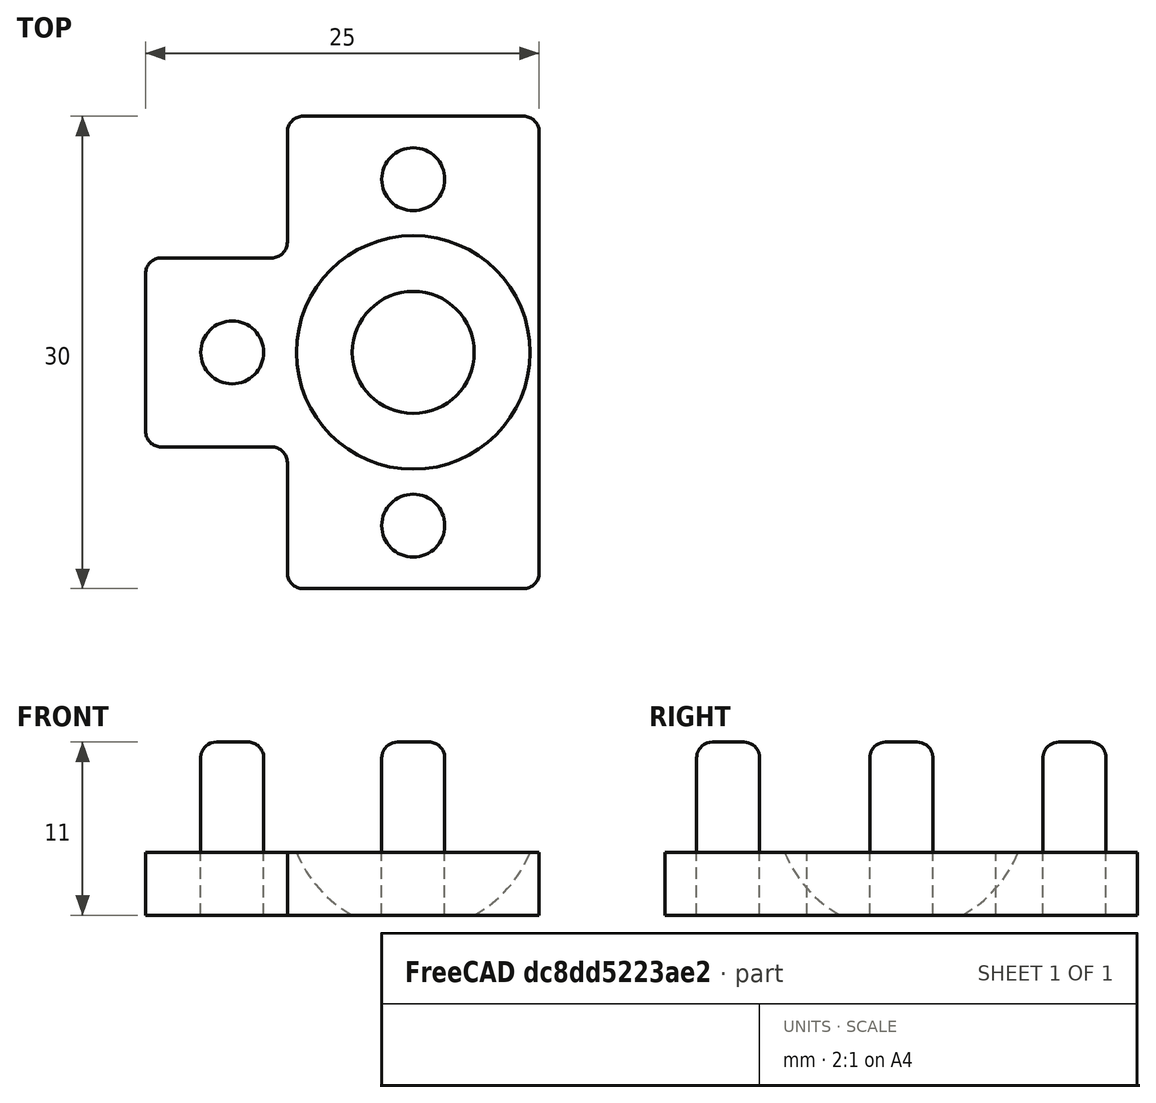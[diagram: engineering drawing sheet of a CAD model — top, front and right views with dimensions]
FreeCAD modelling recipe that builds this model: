
FCSTD DOCUMENT  (FreeCAD 0.20R29603 (Git))
Label: thing for marball
License: All rights reserved
LicenseURL: http://en.wikipedia.org/wiki/All_rights_reserved
objects: Part::Fillet×4, Part::Box×3, Part::Cylinder×3, Part::Cut×3, Part::Sphere×1
note: 14 computed .brp shape members not serialized (recipe doc carries the construction recipe); baked Part::Feature solids carry a one-line shape summary decoded from their .brp

FEATURE [Part::Box] Box  label="Cube"
  AttacherType = Attacher::AttachEngine3D
  Height = 4
  Length = 25
  Width = 30
FEATURE [Part::Sphere] Sphere
  Angle1 = -90
  Angle2 = 90
  Angle3 = 360
  AttacherType = Attacher::AttachEngine3D
  Placement = pos=(17,15,7) rot=(0,0,1;0rad)
  Radius = 8
FEATURE [Part::Cylinder] Cylinder
  Angle = 360
  AttacherType = Attacher::AttachEngine3D
  FirstAngle = 0
  Height = 11
  Placement = pos=(5.5,15,0) rot=(0,0,1;0rad)
  Radius = 2
  SecondAngle = 0
FEATURE [Part::Cylinder] Cylinder001
  Angle = 360
  AttacherType = Attacher::AttachEngine3D
  FirstAngle = 0
  Height = 11
  Placement = pos=(17,26,0) rot=(0,0,1;0rad)
  Radius = 2
  SecondAngle = 0
FEATURE [Part::Cylinder] Cylinder002
  Angle = 360
  AttacherType = Attacher::AttachEngine3D
  FirstAngle = 0
  Height = 11
  Placement = pos=(17,4,0) rot=(0,0,1;0rad)
  Radius = 2
  SecondAngle = 0
FEATURE [Part::Cut] Cut
  Base = -> Box
  Tool = -> Sphere
FEATURE [Part::Box] Box001  label="Cube001"
  AttacherType = Attacher::AttachEngine3D
  Height = 4
  Length = 9
  Width = 9
FEATURE [Part::Box] Box002  label="Cube002"
  AttacherType = Attacher::AttachEngine3D
  Height = 4
  Length = 9
  Placement = pos=(0,21,0) rot=(0,0,1;0rad)
  Width = 9
FEATURE [Part::Cut] Cut001
  Base = -> Cut
  Tool = -> Box001
FEATURE [Part::Cut] Cut002
  Base = -> Cut001
  Tool = -> Box002
FEATURE [Part::Fillet] Fillet
  Base = -> Cut002
  Edges = 8 edges r=1: [Edge2,Edge4,Edge14,Edge22,Edge23,Edge24,Edge25,Edge26]
FEATURE [Part::Fillet] Fillet001
  Base = -> Cylinder
  Edges = 1 edges r=1: [Edge1]
FEATURE [Part::Fillet] Fillet002
  Base = -> Cylinder002
  Edges = 1 edges r=1: [Edge1]
FEATURE [Part::Fillet] Fillet003
  Base = -> Cylinder001
  Edges = 1 edges r=1: [Edge1]
